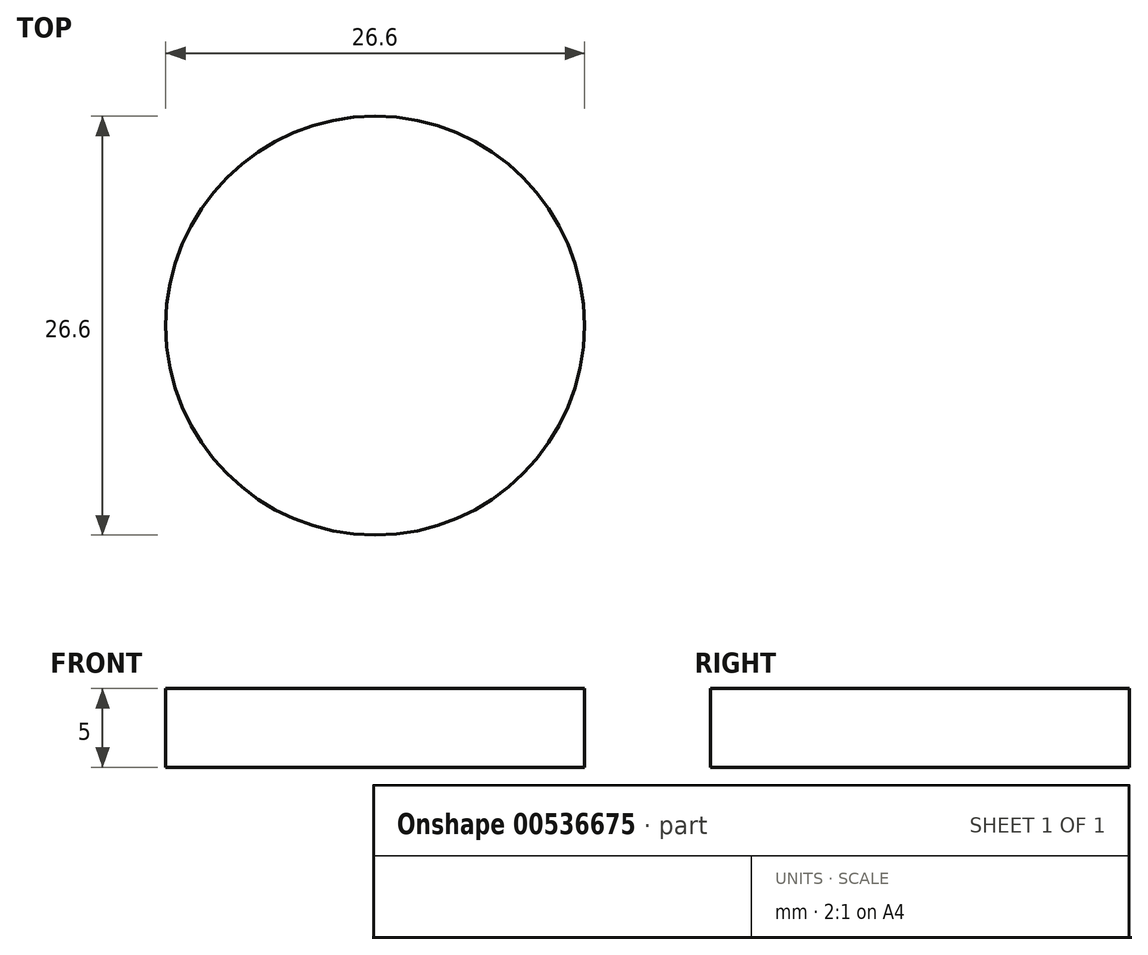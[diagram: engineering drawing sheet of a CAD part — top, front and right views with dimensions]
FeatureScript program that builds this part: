
annotation { "Feature Type Name" : "Feature", "Feature Type Description" : "" }
export const myFeature = defineFeature(function(context is Context, id is Id, definition is map)
    precondition{}
    {
        {
            var Q0;
            Q0=qCreatedBy(makeId("Top.planeOp"),FACE);
            var sketch = newSketch(context, id + "F0", { "sketchPlane" : qUnion([Q0])});
            skCircle(sketch, "E0", {"center": v(0, 0) * mm, "radius": 13.3 * mm});
            skSolve(sketch);
        }
        {
            var Q0;
            Q0=makeQuery(id+"F0.imprint","IMPRINT",FACE,{"disambiguationData":[TD([[makeQuery(id+"F0.imprint","IMPRINT",EDGE,{"derivedFrom":sQuery(id+"F0.wireOp",EDGE,"E0")}),1.0]])]});
            extrude(context, id + "F1", {"entities" : qUnion([Q0]), "depth" : 5 * mm, "offsetDistance" : 25 * mm});
        }
    });
